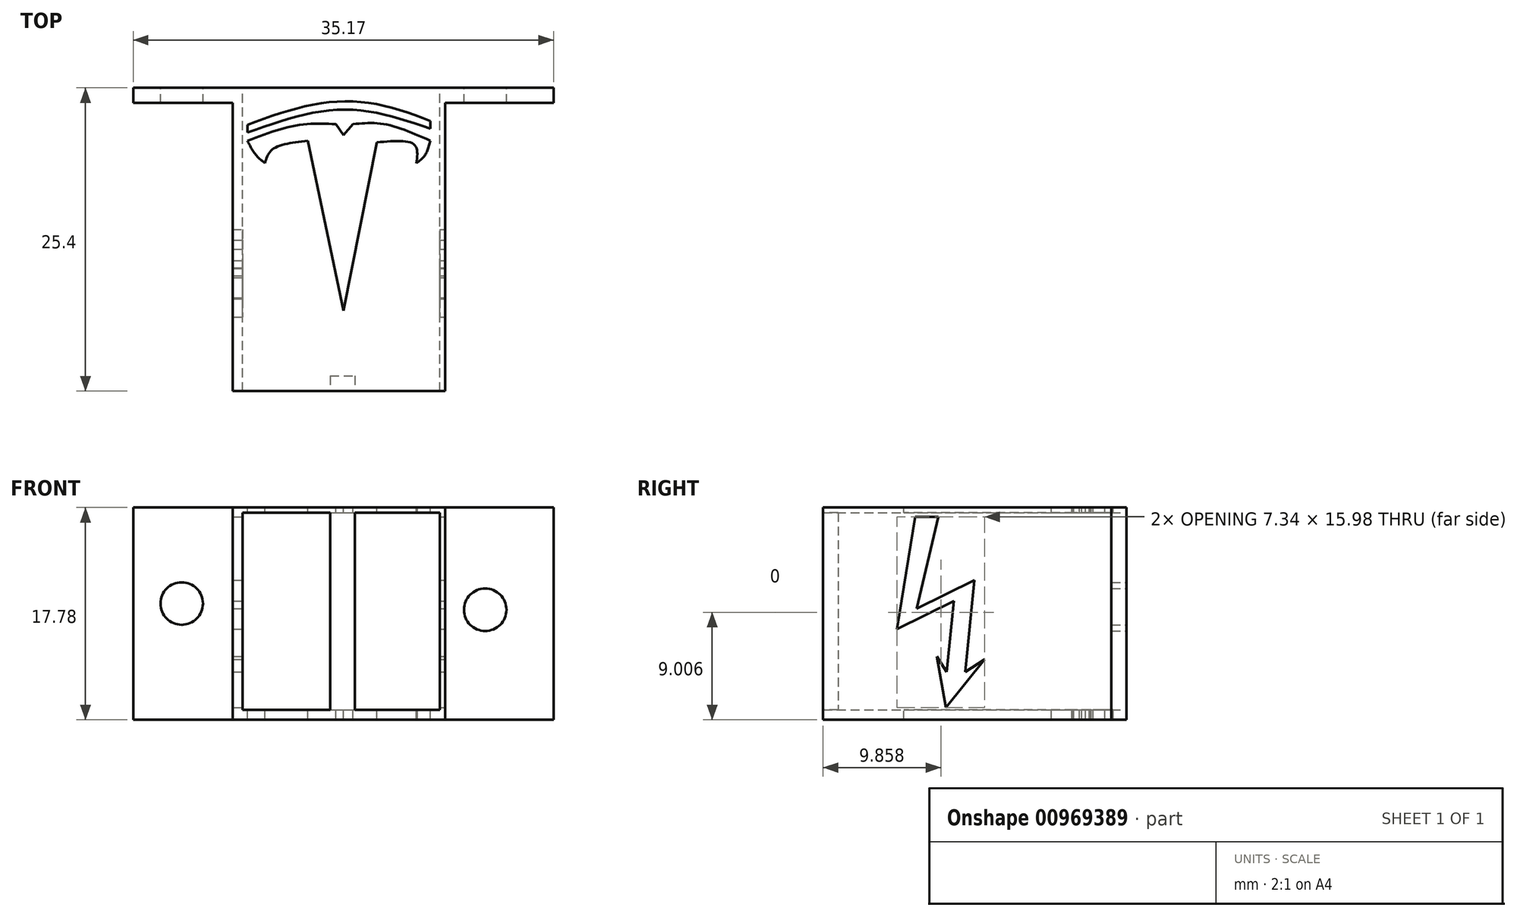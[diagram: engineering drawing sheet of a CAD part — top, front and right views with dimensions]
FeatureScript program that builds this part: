
annotation { "Feature Type Name" : "Feature", "Feature Type Description" : "" }
export const myFeature = defineFeature(function(context is Context, id is Id, definition is map)
    precondition{}
    {
        {
            var Q0;
            Q0=qCreatedBy(makeId("Front.planeOp"),FACE);
            var sketch = newSketch(context, id + "F0", { "sketchPlane" : qUnion([Q0])});
            skLineSegment(sketch, "E0.bottom", {"start": v(-12.7, 0) * mm, "end": v(5.08, 0) * mm});
            skLineSegment(sketch, "E1", {"start": v(-11.03, 17.78) * mm, "end": v(-12.7, 17.78) * mm});
            skLineSegment(sketch, "E2", {"start": v(-1.69, 17.78) * mm, "end": v(5.08, 17.78) * mm});
            skLineSegment(sketch, "E3", {"start": v(-12.7, 17.78) * mm, "end": v(-12.7, 0) * mm});
            skLineSegment(sketch, "E4", {"start": v(5.08, 17.78) * mm, "end": v(5.08, 0) * mm});
            skLineSegment(sketch, "E5", {"start": v(-1.69, 17.78) * mm, "end": v(-11.03, 17.78) * mm});
            skPoint(sketch, "E6.firstSnap0", {"position": v(-11.86, 17.78) * mm});
            skLineSegment(sketch, "E6.bottom", {"start": v(-11.86, 17.34) * mm, "end": v(4.65, 17.34) * mm});
            skLineSegment(sketch, "E6.top", {"start": v(-11.86, 0.83) * mm, "end": v(4.65, 0.83) * mm});
            skLineSegment(sketch, "E6.left", {"start": v(-11.86, 17.34) * mm, "end": v(-11.86, 0.83) * mm});
            skLineSegment(sketch, "E6.right", {"start": v(4.65, 17.34) * mm, "end": v(4.65, 0.83) * mm});
            skPoint(sketch, "E7.endSnap0", {"position": v(-12.7, 8.89) * mm});
            skLineSegment(sketch, "E8", {"start": v(-11.03, 17.78) * mm, "end": v(-21, 17.78) * mm});
            skLineSegment(sketch, "E9", {"start": v(-21, 17.78) * mm, "end": v(-21, 0) * mm});
            skLineSegment(sketch, "E10", {"start": v(-21, 0) * mm, "end": v(14.16, 0) * mm});
            skLineSegment(sketch, "E11", {"start": v(14.16, 0) * mm, "end": v(14.16, 17.78) * mm});
            skLineSegment(sketch, "E12", {"start": v(14.16, 17.78) * mm, "end": v(-11.03, 17.78) * mm});
            skCircle(sketch, "E13", {"center": v(8.44, 9.22) * mm, "radius": 1.78 * mm});
            skCircle(sketch, "E14", {"center": v(-16.96, 9.74) * mm, "radius": 1.78 * mm});
            skLineSegment(sketch, "E15", {"start": v(9.82, 8.1) * mm, "end": v(9.82, 0) * mm});
            skLineSegment(sketch, "E16", {"start": v(-17.62, 8.1) * mm, "end": v(-17.62, 0) * mm});
            skSolve(sketch);
        }
        {
            var Q0;
            {var subQ4=sQuery(id+"F0.wireOp",EDGE,"E3");Q0=makeQuery(id+"F0.imprint","IMPRINT",FACE,{"disambiguationData":[TD([[makeQuery(id+"F0.imprint","IMPRINT",EDGE,{"derivedFrom":subQ4}),1.0]])]});}
            extrude(context, id + "F1", {"entities" : qUnion([Q0]), "depth" : 25.4 * mm, "offsetDistance" : 25.4 * mm});
        }
        {
            var Q0;
            {var subQ0=sQuery(id+"F0.wireOp",EDGE,"E4");Q0=makeQuery(id+"F0.imprint","IMPRINT",FACE,{"disambiguationData":[TD([[makeQuery(id+"F0.imprint","IMPRINT",EDGE,{"derivedFrom":subQ0}),1.0]])]});}
            var Q1;
            {var subQ0=sQuery(id+"F0.wireOp",EDGE,"E3");Q1=makeQuery(id+"F0.imprint","IMPRINT",FACE,{"disambiguationData":[TD([[makeQuery(id+"F0.imprint","IMPRINT",EDGE,{"derivedFrom":subQ0}),-1.0]])]});}
            extrude(context, id + "F2", {"entities" : qUnion([Q0, Q1]), "operationType" : NewBodyOperationType.ADD, "depth" : 1.27 * mm, "offsetDistance" : 25.4 * mm});
        }
        {
            var Q0;
            Q0=makeQuery(id+"F1.opExtrude","CAP_FACE",FACE,{"disambiguationData":[OSD([sQuery(id+"F0.wireOp",EDGE,"E3"),sQuery(id+"F0.wireOp",EDGE,"E4"),sQuery(id+"F0.wireOp",EDGE,"E6.bottom"),sQuery(id+"F0.wireOp",EDGE,"E6.top"),sQuery(id+"F0.wireOp",EDGE,"E6.left"),sQuery(id+"F0.wireOp",EDGE,"E6.right"),sQuery(id+"F0.wireOp",EDGE,"E8"),sQuery(id+"F0.wireOp",EDGE,"E10"),sQuery(id+"F0.wireOp",EDGE,"E12")])],"isStart":false});
            var sketch = newSketch(context, id + "F3", { "sketchPlane" : qUnion([Q0])});
            skLineSegment(sketch, "E17", {"start": v(-4.54, 17.34) * mm, "end": v(-4.54, 0.83) * mm});
            skLineSegment(sketch, "E18", {"start": v(-2.47, 17.34) * mm, "end": v(-2.47, 0.83) * mm});
            skSolve(sketch);
        }
        {
            var Q0;
            {var subQ0=sQuery(id+"F3.wireOp",EDGE,"E17");Q0=makeQuery(id+"F3.imprint","IMPRINT",FACE,{"disambiguationData":[TD([[makeQuery(id+"F3.imprint","IMPRINT",EDGE,{"derivedFrom":subQ0}),1.0]])]});}
            extrude(context, id + "F4", {"entities" : qUnion([Q0]), "operationType" : NewBodyOperationType.ADD, "oppositeDirection" : true, "depth" : 1.27 * mm, "offsetDistance" : 25.4 * mm});
        }
        {
            var Q0;
            {var subQ0=sQuery(id+"F0.wireOp",EDGE,"E12");var subQ1=sQuery(id+"F0.wireOp",EDGE,"E8");Q0=makeQuery(id+"F2.boolean.opBoolean","MERGE",FACE,{"derivedFrom":[makeQuery(id+"F1.opExtrude","SWEPT_FACE",FACE,{"disambiguationData":[OSD([subQ1,subQ0])]}),makeQuery(id+"F2.opExtrude","SWEPT_FACE",FACE,{"disambiguationData":[OSD([subQ1])]}),makeQuery(id+"F2.opExtrude","SWEPT_FACE",FACE,{"disambiguationData":[OSD([subQ0])]})]});}
            var sketch = newSketch(context, id + "F5", { "sketchPlane" : qUnion([Q0])});
            skPoint(sketch, "E19.1.internal.snap0", {"position": v(-3.42, 0) * mm});
            skFitSpline(sketch, "E19", {"points": [v(-11.46, -3.1) * mm, v(-3.42, -1.13) * mm, v(3.84, -2.8) * mm], "startDerivative": vector(15.92, 6.1) * mm, "endDerivative": vector(14.69, -6.2) * mm});
            skLineSegment(sketch, "E20", {"start": v(-11.46, -3.1) * mm, "end": v(-11.46, -3.74) * mm});
            skPoint(sketch, "E21.2.internal.snap0", {"position": v(-11.46, -3.43) * mm});
            skFitSpline(sketch, "E21", {"points": [v(-11.46, -3.74) * mm, v(-3.42, -1.82) * mm, v(3.84, -3.43) * mm], "startDerivative": vector(15.87, 5.58) * mm, "endDerivative": vector(14.74, -5.11) * mm});
            skLineSegment(sketch, "E22", {"start": v(3.84, -3.43) * mm, "end": v(3.84, -2.8) * mm});
            skFitSpline(sketch, "E23", {"points": [v(-11.46, -4.43) * mm, v(-7.3, -3.14) * mm, v(-4.07, -3.04) * mm], "startDerivative": vector(7.97, 2.99) * mm, "endDerivative": vector(6.8, -0.3) * mm});
            skLineSegment(sketch, "E24", {"start": v(-4.07, -3.04) * mm, "end": v(-3.42, -3.94) * mm});
            skLineSegment(sketch, "E25", {"start": v(-3.42, -3.94) * mm, "end": v(-2.61, -3.04) * mm});
            skFitSpline(sketch, "E26", {"points": [v(-2.61, -3.04) * mm, v(0, -3.04) * mm, v(3.84, -4.43) * mm], "startDerivative": vector(5.65, 0.55) * mm, "endDerivative": vector(7.2, -3.19) * mm});
            skFitSpline(sketch, "E27", {"points": [v(-11.46, -4.43) * mm, v(-10.73, -5.65) * mm, v(-9.99, -6.3) * mm], "startDerivative": vector(1.27, -2.46) * mm, "endDerivative": vector(1.7, -1.24) * mm});
            skFitSpline(sketch, "E28", {"points": [v(-9.99, -6.3) * mm, v(-9.38, -5.17) * mm, v(-6.41, -4.43) * mm], "startDerivative": vector(0.9, 3.2) * mm, "endDerivative": vector(5.9, 0.72) * mm});
            skLineSegment(sketch, "E29", {"start": v(-6.41, -4.43) * mm, "end": v(-3.42, -18.65) * mm});
            skLineSegment(sketch, "E30", {"start": v(-3.42, -18.65) * mm, "end": v(-0.64, -4.57) * mm});
            skFitSpline(sketch, "E31", {"points": [v(3.84, -4.43) * mm, v(3.4, -5.65) * mm, v(2.69, -6.3) * mm], "startDerivative": vector(-0.65, -2.5) * mm, "endDerivative": vector(-1.69, -1.2) * mm});
            skFitSpline(sketch, "E32", {"points": [v(2.69, -6.3) * mm, v(2.5, -4.77) * mm, v(-0.64, -4.57) * mm], "startDerivative": vector(0.57, 4.4) * mm, "endDerivative": vector(-6.78, -0.65) * mm});
            skSolve(sketch);
        }
        {
            var Q0;
            Q0=makeQuery(id+"F5.imprint","IMPRINT",FACE,{"disambiguationData":[TD([[makeQuery(id+"F5.imprint","IMPRINT",EDGE,{"derivedFrom":sQuery(id+"F5.wireOp",EDGE,"E23")}),-1.0]])]});
            extrude(context, id + "F6", {"entities" : qUnion([Q0]), "operationType" : NewBodyOperationType.REMOVE, "oppositeDirection" : true, "depth" : 25.4 * mm, "offsetDistance" : 25.4 * mm});
        }
        {
            var Q0;
            Q0=makeQuery(id+"F5.imprint","IMPRINT",FACE,{"disambiguationData":[TD([[makeQuery(id+"F5.imprint","IMPRINT",EDGE,{"derivedFrom":sQuery(id+"F5.wireOp",EDGE,"E19")}),-1.0]])]});
            extrude(context, id + "F7", {"entities" : qUnion([Q0]), "operationType" : NewBodyOperationType.REMOVE, "oppositeDirection" : true, "depth" : 25.4 * mm, "offsetDistance" : 25.4 * mm});
        }
        {
            var Q0;
            Q0=makeQuery(id+"F1.opExtrude","SWEPT_FACE",FACE,{"disambiguationData":[OSD([sQuery(id+"F0.wireOp",EDGE,"E4")])]});
            var sketch = newSketch(context, id + "F8", { "sketchPlane" : qUnion([Q0])});
            skLineSegment(sketch, "E33", {"start": v(-17.68, 17) * mm, "end": v(-19.21, 7.61) * mm});
            skLineSegment(sketch, "E34", {"start": v(-19.21, 7.61) * mm, "end": v(-14.46, 9.96) * mm});
            skLineSegment(sketch, "E35", {"start": v(-14.46, 9.96) * mm, "end": v(-15.06, 4.01) * mm});
            skLineSegment(sketch, "E36", {"start": v(-15.06, 4.01) * mm, "end": v(-15.89, 5.33) * mm});
            skLineSegment(sketch, "E37", {"start": v(-15.89, 5.33) * mm, "end": v(-15.13, 1.02) * mm});
            skLineSegment(sketch, "E38", {"start": v(-15.13, 1.02) * mm, "end": v(-11.87, 5.05) * mm});
            skLineSegment(sketch, "E39", {"start": v(-11.87, 5.05) * mm, "end": v(-13.5, 4.01) * mm});
            skLineSegment(sketch, "E40", {"start": v(-13.5, 4.01) * mm, "end": v(-12.74, 11.7) * mm});
            skLineSegment(sketch, "E41", {"start": v(-12.74, 11.7) * mm, "end": v(-17.57, 9.31) * mm});
            skLineSegment(sketch, "E42", {"start": v(-17.57, 9.31) * mm, "end": v(-15.75, 17) * mm});
            skLineSegment(sketch, "E43", {"start": v(-15.75, 17) * mm, "end": v(-17.68, 17) * mm});
            skSolve(sketch);
        }
        {
            var Q0;
            Q0 = qSketchRegion(id + "F8", true);
            extrude(context, id + "F9", {"entities" : qUnion([Q0]), "operationType" : NewBodyOperationType.REMOVE, "oppositeDirection" : true, "depth" : 25.4 * mm, "offsetDistance" : 25.4 * mm});
        }
    });
